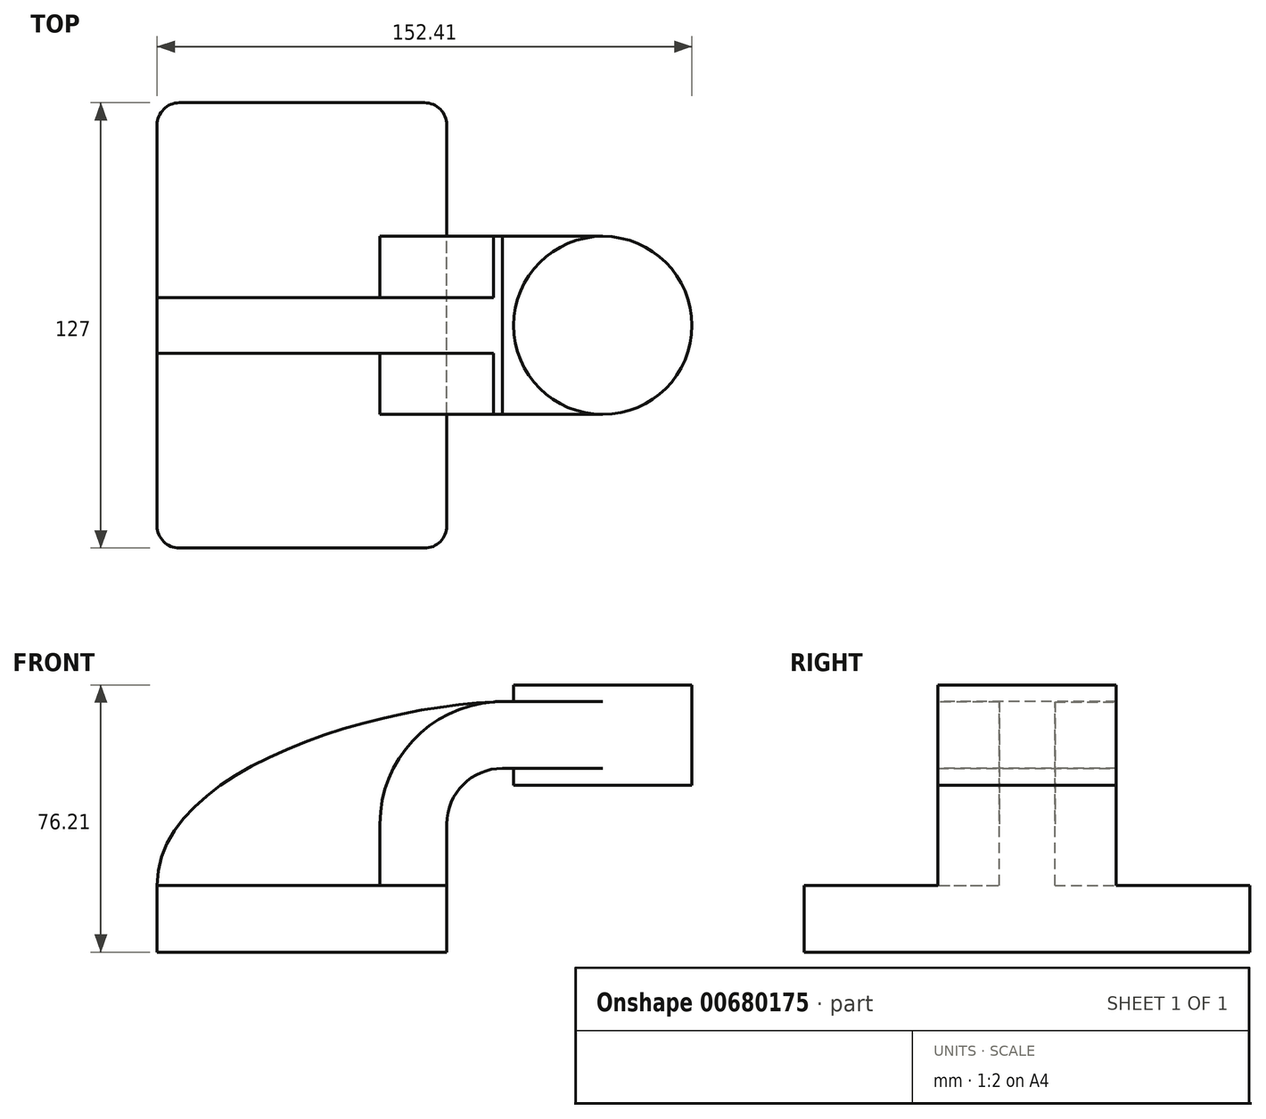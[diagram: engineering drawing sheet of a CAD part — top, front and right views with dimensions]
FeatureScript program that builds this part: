
annotation { "Feature Type Name" : "Feature", "Feature Type Description" : "" }
export const myFeature = defineFeature(function(context is Context, id is Id, definition is map)
    precondition{}
    {
        {
            var Q0;
            Q0=qCreatedBy(makeId("Front.planeOp"),FACE);
            var sketch = newSketch(context, id + "F0", { "sketchPlane" : qUnion([Q0])});
            skLineSegment(sketch, "E0.bottom", {"start": v(41.27, 9.53) * mm, "end": v(-41.28, 9.52) * mm});
            skLineSegment(sketch, "E0.top", {"start": v(41.28, -9.52) * mm, "end": v(-41.28, -9.53) * mm});
            skLineSegment(sketch, "E0.left", {"start": v(41.27, 9.53) * mm, "end": v(41.28, -9.52) * mm});
            skLineSegment(sketch, "E0.right", {"start": v(-41.28, 9.52) * mm, "end": v(-41.28, -9.53) * mm});
            skPoint(sketch, "E0.middle", {"position": v(0, 0) * mm});
            skLineSegment(sketch, "E1.bottom", {"start": v(111.12, 66.68) * mm, "end": v(60.32, 66.67) * mm});
            skLineSegment(sketch, "E1.top", {"start": v(111.12, 38.1) * mm, "end": v(60.32, 38.1) * mm});
            skLineSegment(sketch, "E1.left", {"start": v(111.12, 66.68) * mm, "end": v(111.12, 38.1) * mm});
            skLineSegment(sketch, "E1.right", {"start": v(60.32, 66.67) * mm, "end": v(60.32, 38.1) * mm});
            skPoint(sketch, "E1.middle", {"position": v(85.72, 52.39) * mm});
            skLineSegment(sketch, "E2", {"start": v(41.27, 9.53) * mm, "end": v(41.27, 27) * mm});
            skArc(sketch, "E3", {"start": v(41.27, 27) * mm, "mid": v(45.92, 38.23) * mm, "end": v(57.15, 42.88) * mm});
            skLineSegment(sketch, "E4", {"start": v(57.15, 42.88) * mm, "end": v(85.72, 42.88) * mm});
            skLineSegment(sketch, "E5.0", {"start": v(57.15, 61.93) * mm, "end": v(85.72, 61.93) * mm});
            skArc(sketch, "E5.1", {"start": v(22.22, 27) * mm, "mid": v(32.45, 51.7) * mm, "end": v(57.15, 61.93) * mm});
            skLineSegment(sketch, "E5.2", {"start": v(22.23, 9.52) * mm, "end": v(22.23, 27) * mm});
            skFitSpline(sketch, "E6", {"points": [v(-41.28, 9.52) * mm, v(57.15, 61.93) * mm], "startDerivative": vector(-0.95, 98.95) * mm, "endDerivative": vector(107.21, 2.73) * mm});
            skLineSegment(sketch, "E7", {"start": v(85.72, 66.67) * mm, "end": v(85.72, 38.1) * mm});
            skSolve(sketch);
        }
        {
            var Q0;
            Q0=makeQuery(id+"F0.imprint","IMPRINT",FACE,{"disambiguationData":[TD([[makeQuery(id+"F0.imprint","IMPRINT",EDGE,{"derivedFrom":sQuery(id+"F0.wireOp",EDGE,"E0.top")}),-1.0]])]});
            extrude(context, id + "F1", {"entities" : qUnion([Q0]), "endBound" : BoundingType.SYMMETRIC, "depth" : 127 * mm, "offsetDistance" : 25.4 * mm});
        }
        {
            var Q0;
            {var subQ3=sQuery(id+"F0.wireOp",EDGE,"E5.2");Q0=makeQuery(id+"F0.imprint","IMPRINT",FACE,{"disambiguationData":[TD([[makeQuery(id+"F0.imprint","IMPRINT",EDGE,{"derivedFrom":subQ3}),1.0]])]});}
            extrude(context, id + "F2", {"entities" : qUnion([Q0]), "operationType" : NewBodyOperationType.ADD, "endBound" : BoundingType.SYMMETRIC, "depth" : 15.88 * mm, "offsetDistance" : 25.4 * mm});
        }
        {
            var Q0;
            {var subQ1=sQuery(id+"F0.wireOp",EDGE,"E2");Q0=makeQuery(id+"F0.imprint","IMPRINT",FACE,{"disambiguationData":[TD([[makeQuery(id+"F0.imprint","IMPRINT",EDGE,{"derivedFrom":subQ1}),1.0]])]});}
            var Q1;
            {var subQ0=sQuery(id+"F0.wireOp",EDGE,"E5.0");var subQ1=sQuery(id+"F0.wireOp",EDGE,"E1.right");var subQ2=makeQuery(id+"F0.imprint","INTERSECT",VERTEX,{"derivedFrom":[subQ1,subQ0]});Q1=makeQuery(id+"F0.imprint","IMPRINT",FACE,{"disambiguationData":[TD([[makeQuery(id+"F0.imprint","IMPRINT",EDGE,{"disambiguationData":[TD([[subQ2,-1.0]])],"derivedFrom":subQ1}),1.0]])]});}
            extrude(context, id + "F3", {"entities" : qUnion([Q0, Q1]), "operationType" : NewBodyOperationType.ADD, "endBound" : BoundingType.SYMMETRIC, "depth" : 50.8 * mm, "offsetDistance" : 25.4 * mm});
        }
        {
            var Q0;
            {var subQ4=sQuery(id+"F0.wireOp",EDGE,"E1.left");Q0=makeQuery(id+"F0.imprint","IMPRINT",FACE,{"disambiguationData":[TD([[makeQuery(id+"F0.imprint","IMPRINT",EDGE,{"derivedFrom":subQ4}),-1.0]])]});}
            var Q1;
            Q1=sQuery(id+"F0.wireOp",EDGE,"E7");
            revolve(context, id + "F4", {"operationType" : NewBodyOperationType.ADD, "entities" : qUnion([Q0]), "axis" : qUnion([Q1]), "revolveType" : RevolveType.FULL});
        }
        {
            var Q0;
            Q0=makeQuery(id+"F1.opExtrude","CAP_EDGE",EDGE,{"disambiguationData":[OSD([sQuery(id+"F0.wireOp",EDGE,"E0.left")])],"isStart":false});
            var Q1;
            Q1=makeQuery(id+"F1.opExtrude","CAP_EDGE",EDGE,{"disambiguationData":[OSD([sQuery(id+"F0.wireOp",EDGE,"E0.right")])],"isStart":false});
            var Q2;
            Q2=makeQuery(id+"F1.opExtrude","CAP_EDGE",EDGE,{"disambiguationData":[OSD([sQuery(id+"F0.wireOp",EDGE,"E0.left")])],"isStart":true});
            var Q3;
            Q3=makeQuery(id+"F1.opExtrude","CAP_EDGE",EDGE,{"disambiguationData":[OSD([sQuery(id+"F0.wireOp",EDGE,"E0.right")])],"isStart":true});
            fillet(context, id + "F5", {"entities" : qUnion([Q0, Q1, Q2, Q3]), "radius" : 6.35 * mm, "tangentPropagation" : true, "allowEdgeOverflow" : false});
        }
    });
